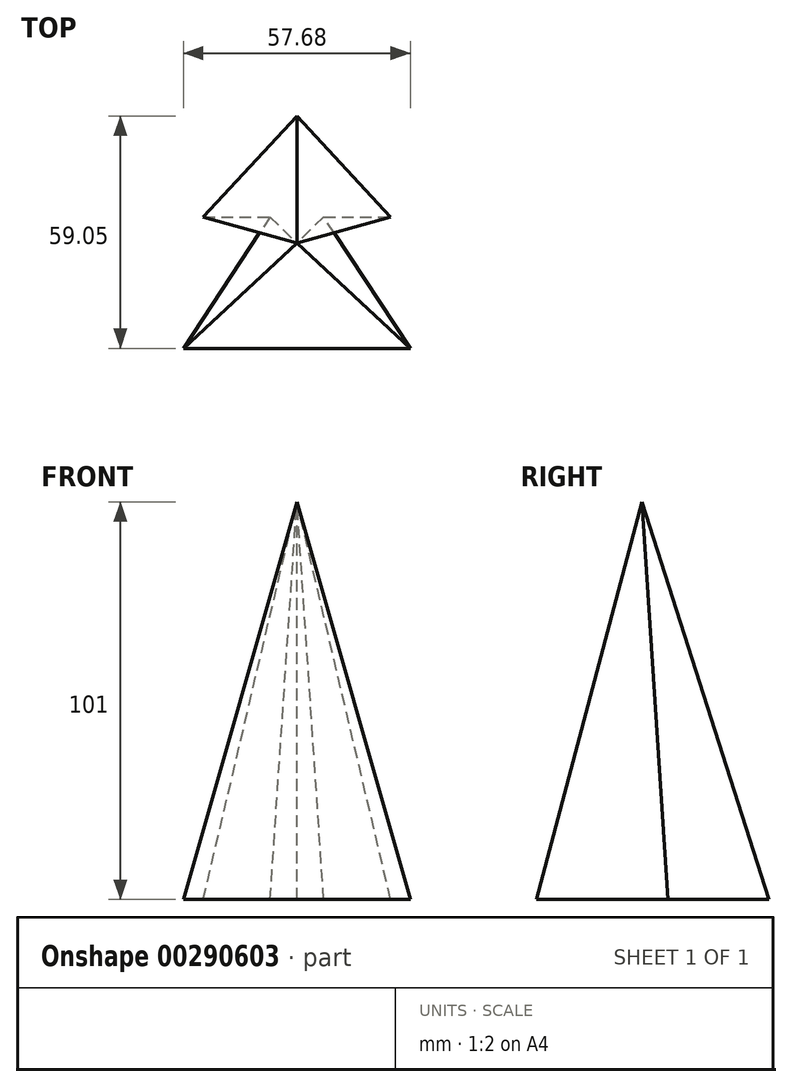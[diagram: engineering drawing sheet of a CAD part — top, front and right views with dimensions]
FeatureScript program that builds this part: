
annotation { "Feature Type Name" : "Feature", "Feature Type Description" : "" }
export const myFeature = defineFeature(function(context is Context, id is Id, definition is map)
    precondition{}
    {
        {
            var Q0;
            Q0=qCreatedBy(makeId("Top.planeOp"),FACE);
            var sketch = newSketch(context, id + "F0", { "sketchPlane" : qUnion([Q0])});
            skLineSegment(sketch, "E0", {"start": v(0, 43.34) * mm, "end": v(-23.8, 17.67) * mm});
            skLineSegment(sketch, "E1", {"start": v(-23.8, 17.67) * mm, "end": v(-6.8, 17.67) * mm});
            skLineSegment(sketch, "E2", {"start": v(-6.8, 17.67) * mm, "end": v(-28.84, -15.7) * mm});
            skLineSegment(sketch, "E3", {"start": v(-28.84, -15.7) * mm, "end": v(28.84, -15.7) * mm});
            skLineSegment(sketch, "E4", {"start": v(28.84, -15.7) * mm, "end": v(6.8, 17.67) * mm});
            skLineSegment(sketch, "E5", {"start": v(6.8, 17.67) * mm, "end": v(23.8, 17.67) * mm});
            skLineSegment(sketch, "E6", {"start": v(23.8, 17.67) * mm, "end": v(0, 43.34) * mm});
            skSolve(sketch);
        }
        {
            var Q0;
            Q0=qCreatedBy(makeId("Top.planeOp"),FACE);
            cPlane(context, id + "F1", {"entities" : qUnion([Q0]), "cplaneType" : CPlaneType.OFFSET, "offset" : 101 * mm, "width" : 150 * mm, "height" : 150 * mm});
        }
        {
            var Q0;
            Q0=qCreatedBy(id+"F1.planeOp",FACE);
            var sketch = newSketch(context, id + "F2", { "sketchPlane" : qUnion([Q0])});
            skPoint(sketch, "E7", {"position": v(0, 11.05) * mm});
            skSolve(sketch);
        }
        {
            var Q0;
            Q0=makeQuery(id+"F0.imprint","IMPRINT",FACE,{"disambiguationData":[TD([[makeQuery(id+"F0.imprint","IMPRINT",EDGE,{"derivedFrom":sQuery(id+"F0.wireOp",EDGE,"E0")}),1.0]])]});
            var Q1;
            Q1=sQuery(id+"F2.wireOp",VERTEX,"E7");
            loft(context, id + "F3", {"sheetProfilesArray" : [{ "sheetProfileEntities" : qUnion([Q0]) }, { "sheetProfileEntities" : qUnion([Q1]) }]});
        }
    });
